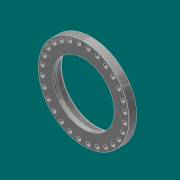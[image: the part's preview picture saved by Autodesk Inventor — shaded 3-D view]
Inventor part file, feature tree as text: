
AUTODESK INVENTOR PART (.ipt)
format: ipt  version: 2017.3 (Build 213257000, 257)  size: 356,864 bytes
history: native  units: in
note: dims shown in document units (in); Inventor stores cm internally (conversion verified against a paired STEP export)
features: sketch x6, extrude x4, chamfer x4, fillet x2, hole x1, pattern_circular x1, revolve x1, projected_geometry x1
ambient origin geometry x8: Origin, YZ Plane, XZ Plane, XY Plane, X Axis, Y Axis, Z Axis, Center Point
bodies: Solid1 (feature_tree)
feature tree (20):
  extrude  "Extrusion1"  Depth=29.0in
  extrude  "Extrusion2"  Depth=33.75in
  extrude  "Extrusion3"  Depth=34.75in
  extrude  "Extrusion9"  Depth=19.625in
  hole  "Hole1"  [1 undecoded]
  chamfer  "Chamfer3"  Distance=0.125in
  pattern_circular  "Circular Pattern1"  [2 undecoded]
  chamfer  "Chamfer2"  Distance=0.0312in Angle=45.0deg
  fillet  "Fillet2"  Radius=0.125in
  chamfer  "Chamfer4"  Distance=34.0in
  revolve  "Revolution3"  [1 undecoded]
  fillet  "Fillet7"  Radius=0.125in
  chamfer  "Chamfer8"  Distance=0.25in
  sketch  "Sketch1"  dims[d0=43.0in d1=29.0in]
  sketch  "Sketch2"  dims[d2=3.625in d3=0.0in d4=33.75in]
  sketch  "Sketch3"  dims[d5=0.0625in d6=0.0in d7=34.75in]
  sketch  "Sketch4"  dims[d8=2.4375in d9=0.0in d13=19.625in]
  sketch  "Sketch12"  dims[d14=0.0442in]
  sketch  "Sketch15"  dims[d15=1.875in d16=0.75in d17=0.375in d18=0.25in d19=0.5635in d20=1.0in d21=0.8108in d22=11.0236in d23=360.0deg d25=0.0625in d26=0.125in d27=0.0687in d29=0.4375in d30=0.0312in d31=0.125in d32=45.0deg d33=0.0625in d34=0.125in d35=45.0deg d98=34.0in d99=0.3125in d100=0.125in d101=0.25in d102=0.2577in d103=0.5in d104=0.875in d105=0.3852in d106=29.375in d108=90.0deg d109=0.0312in d110=0.0312in d111=0.125in d112=45.0deg d120=1.0in d129=1.0in d130=0.0in d134=0.0625in d135=0.1718in]
  projected_geometry  "Projected Loop1"
note: 4 required parameter values undecoded (feature->parameter linkage not recoverable at this tier; creation-order binding heuristic only, values carry confidence <= 0.55)